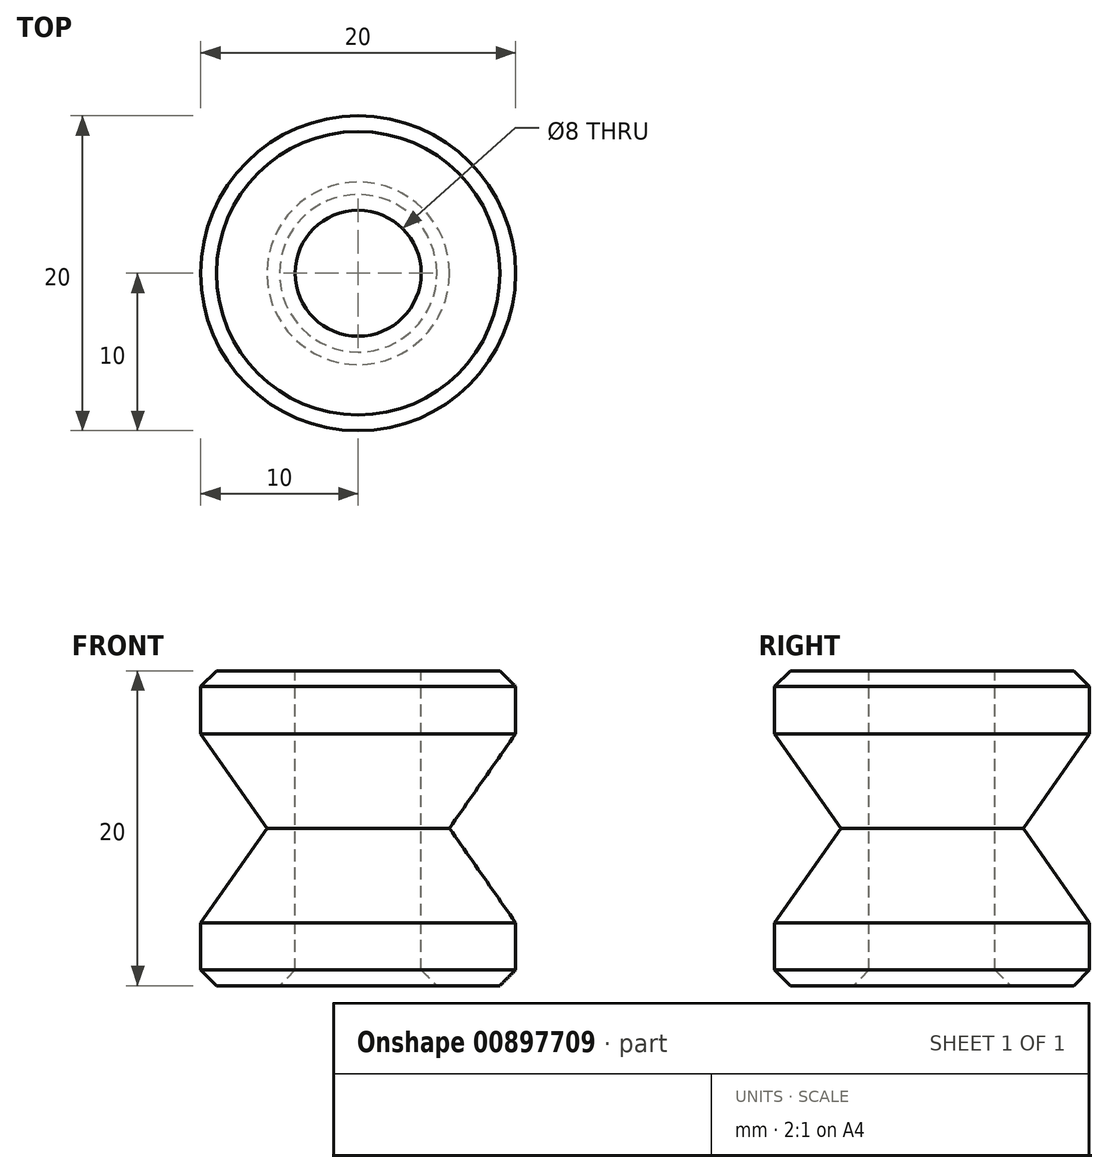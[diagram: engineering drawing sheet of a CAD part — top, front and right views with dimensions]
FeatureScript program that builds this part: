
annotation { "Feature Type Name" : "Feature", "Feature Type Description" : "" }
export const myFeature = defineFeature(function(context is Context, id is Id, definition is map)
    precondition{}
    {
        {
            var Q0;
            Q0=qCreatedBy(makeId("Top.planeOp"),FACE);
            var sketch = newSketch(context, id + "F0", { "sketchPlane" : qUnion([Q0])});
            skCircle(sketch, "E0", {"center": v(0, 0) * mm, "radius": 10 * mm});
            skSolve(sketch);
        }
        {
            var Q0;
            Q0 = qSketchRegion(id + "F0", true);
            extrude(context, id + "F1", {"entities" : qUnion([Q0]), "oppositeDirection" : true, "depth" : 20 * mm, "offsetDistance" : 25 * mm});
        }
        {
            var Q0;
            Q0=qCreatedBy(makeId("Right.planeOp"),FACE);
            var sketch = newSketch(context, id + "F2", { "sketchPlane" : qUnion([Q0])});
            skLineSegment(sketch, "E1", {"start": v(18.16, -10) * mm, "end": v(-19.8, -10) * mm, "construction": true});
            skLineSegment(sketch, "E2", {"start": v(10, 0) * mm, "end": v(10, -20) * mm});
            skLineSegment(sketch, "E3", {"start": v(10, -4) * mm, "end": v(10, -16) * mm, "construction": true});
            skLineSegment(sketch, "E4", {"start": v(10, 0) * mm, "end": v(10, -20) * mm, "construction": true});
            skLineSegment(sketch, "E5", {"start": v(10, -4) * mm, "end": v(5.8, -10) * mm});
            skLineSegment(sketch, "E6", {"start": v(5.8, -10) * mm, "end": v(10, -16) * mm});
            skSolve(sketch);
        }
        {
            var Q0;
            Q0 = qSketchRegion(id + "F2", true);
            var Q1;
            Q1=makeQuery(id+"F1.opExtrude","SWEPT_FACE",FACE,{"disambiguationData":[OSD([sQuery(id+"F0.wireOp",EDGE,"E0")])]});
            revolve(context, id + "F3", {"operationType" : NewBodyOperationType.REMOVE, "surfaceOperationType" : NewSurfaceOperationType.NEW, "entities" : qUnion([Q0]), "axis" : qUnion([Q1]), "revolveType" : RevolveType.FULL, "oppositeDirection" : true});
        }
        {
            var Q0;
            Q0=makeQuery(id+"F1.opExtrude","CAP_FACE",FACE,{"disambiguationData":[OSD([sQuery(id+"F0.wireOp",EDGE,"E0")])],"isStart":true});
            var sketch = newSketch(context, id + "F4", { "sketchPlane" : qUnion([Q0])});
            skSolve(sketch);
        }
        {
            var Q0;
            Q0=makeQuery(id+"F4.imprint","IMPRINT",FACE,{"disambiguationData":[TD([[makeQuery(id+"F4.imprint","IMPRINT",EDGE,{"derivedFrom":makeQuery(id+"F1.opExtrude","CAP_EDGE",EDGE,{"disambiguationData":[OSD([sQuery(id+"F0.wireOp",EDGE,"E0")])],"isStart":true})}),1.0]])]});
            var sketch = newSketch(context, id + "F5", { "sketchPlane" : qUnion([Q0])});
            skCircle(sketch, "E7", {"center": v(0, 0) * mm, "radius": 4 * mm});
            skSolve(sketch);
        }
        {
            var Q0;
            Q0 = qSketchRegion(id + "F5", true);
            extrude(context, id + "F6", {"entities" : qUnion([Q0]), "operationType" : NewBodyOperationType.REMOVE, "oppositeDirection" : true, "depth" : 25 * mm, "offsetDistance" : 25 * mm});
        }
        {
            var Q0;
            Q0=makeQuery(id+"F6.boolean.opBoolean","INTERSECT",EDGE,{"derivedFrom":[makeQuery(id+"F1.opExtrude","CAP_FACE",FACE,{"disambiguationData":[OSD([sQuery(id+"F0.wireOp",EDGE,"E0")])],"isStart":false}),makeQuery(id+"F6.opExtrude","SWEPT_FACE",FACE,{"disambiguationData":[OSD([sQuery(id+"F5.wireOp",EDGE,"E7")])]})]});
            var Q1;
            Q1=makeQuery(id+"F1.opExtrude","CAP_EDGE",EDGE,{"disambiguationData":[OSD([sQuery(id+"F0.wireOp",EDGE,"E0")])],"isStart":false});
            var Q2;
            Q2=makeQuery(id+"F1.opExtrude","CAP_EDGE",EDGE,{"disambiguationData":[OSD([sQuery(id+"F0.wireOp",EDGE,"E0")])],"isStart":true});
            var Q3;
            Q3=makeQuery(id+"F6.boolean.opBoolean","COPY",EDGE,{"derivedFrom":makeQuery(id+"F6.opExtrude","CAP_EDGE",EDGE,{"disambiguationData":[OSD([sQuery(id+"F5.wireOp",EDGE,"E7")])],"isStart":true})});
            chamfer(context, id + "F7", {"entities" : qUnion([Q0, Q1, Q2, Q3]), "width" : 1 * mm, "tangentPropagation" : true});
        }
        {
            var Q0;
            Q0=makeQuery(id+"F4.imprint","IMPRINT",FACE,{"disambiguationData":[TD([[makeQuery(id+"F4.imprint","IMPRINT",EDGE,{"derivedFrom":makeQuery(id+"F1.opExtrude","CAP_EDGE",EDGE,{"disambiguationData":[OSD([sQuery(id+"F0.wireOp",EDGE,"E0")])],"isStart":true})}),1.0]])]});
            cPlane(context, id + "F8", {"entities" : qUnion([Q0]), "cplaneType" : CPlaneType.OFFSET, "offset" : 11.8 * mm, "width" : 150 * mm, "height" : 150 * mm});
        }
    });
